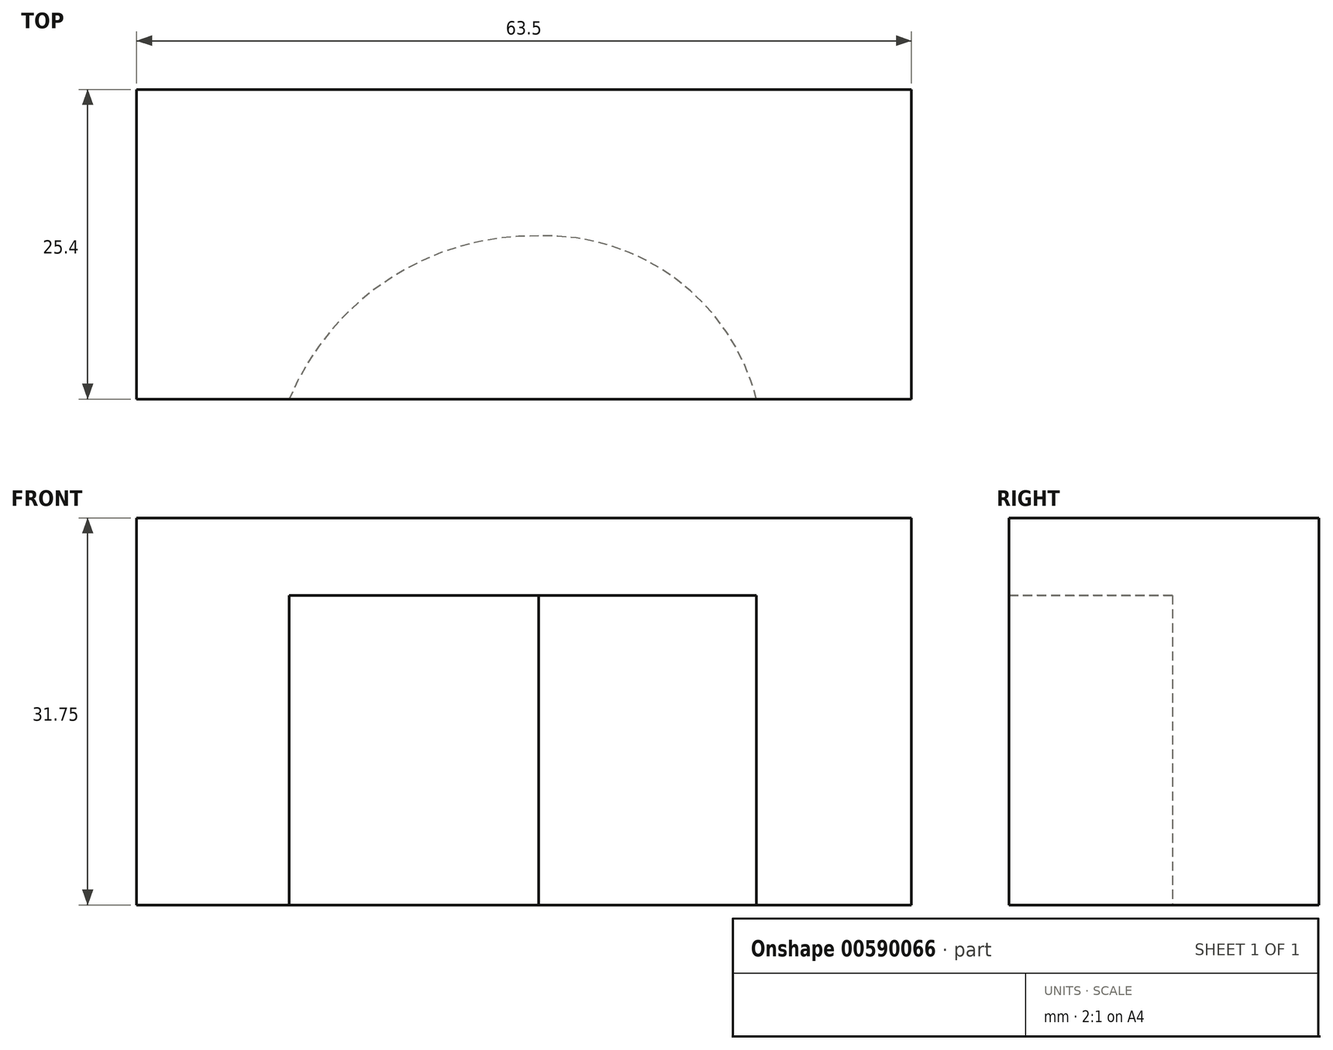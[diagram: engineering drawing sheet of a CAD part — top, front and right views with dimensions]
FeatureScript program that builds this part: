
annotation { "Feature Type Name" : "Feature", "Feature Type Description" : "" }
export const myFeature = defineFeature(function(context is Context, id is Id, definition is map)
    precondition{}
    {
        {
            var Q0;
            Q0=qCreatedBy(makeId("Top.planeOp"),FACE);
            var sketch = newSketch(context, id + "F0", { "sketchPlane" : qUnion([Q0])});
            skLineSegment(sketch, "E0", {"start": v(0, 0) * mm, "end": v(0, 25.4) * mm});
            skLineSegment(sketch, "E1", {"start": v(0, 0) * mm, "end": v(-63.5, 0) * mm});
            skLineSegment(sketch, "E2", {"start": v(0, 25.4) * mm, "end": v(-63.5, 25.4) * mm});
            skLineSegment(sketch, "E3", {"start": v(-63.5, 25.4) * mm, "end": v(-63.5, 0) * mm});
            skSolve(sketch);
        }
        {
            var Q0;
            Q0 = qSketchRegion(id + "F0", true);
            extrude(context, id + "F1", {"entities" : qUnion([Q0]), "depth" : 31.75 * mm, "offsetDistance" : 25.4 * mm});
        }
        {
            var Q0;
            Q0=makeQuery(id+"F1.opExtrude","CAP_FACE",FACE,{"disambiguationData":[OSD([sQuery(id+"F0.wireOp",EDGE,"E0"),sQuery(id+"F0.wireOp",EDGE,"E1"),sQuery(id+"F0.wireOp",EDGE,"E2"),sQuery(id+"F0.wireOp",EDGE,"E3")])],"isStart":true});
            var sketch = newSketch(context, id + "F2", { "sketchPlane" : qUnion([Q0])});
            skArc(sketch, "E4", {"start": v(-30.54, -13.38) * mm, "mid": v(-19.27, -9.82) * mm, "end": v(-12.7, 0) * mm});
            skArc(sketch, "E5", {"start": v(-50.98, 0) * mm, "mid": v(-42.82, -9.83) * mm, "end": v(-30.54, -13.38) * mm});
            skSolve(sketch);
        }
        {
            var Q0;
            {var subQ0=sQuery(id+"F2.wireOp",EDGE,"E4");Q0=makeQuery(id+"F2.imprint","IMPRINT",FACE,{"disambiguationData":[TD([[makeQuery(id+"F2.imprint","IMPRINT",EDGE,{"derivedFrom":subQ0}),1.0]])]});}
            extrude(context, id + "F3", {"entities" : qUnion([Q0]), "operationType" : NewBodyOperationType.REMOVE, "oppositeDirection" : true, "depth" : 25.4 * mm, "offsetDistance" : 25.4 * mm});
        }
    });
